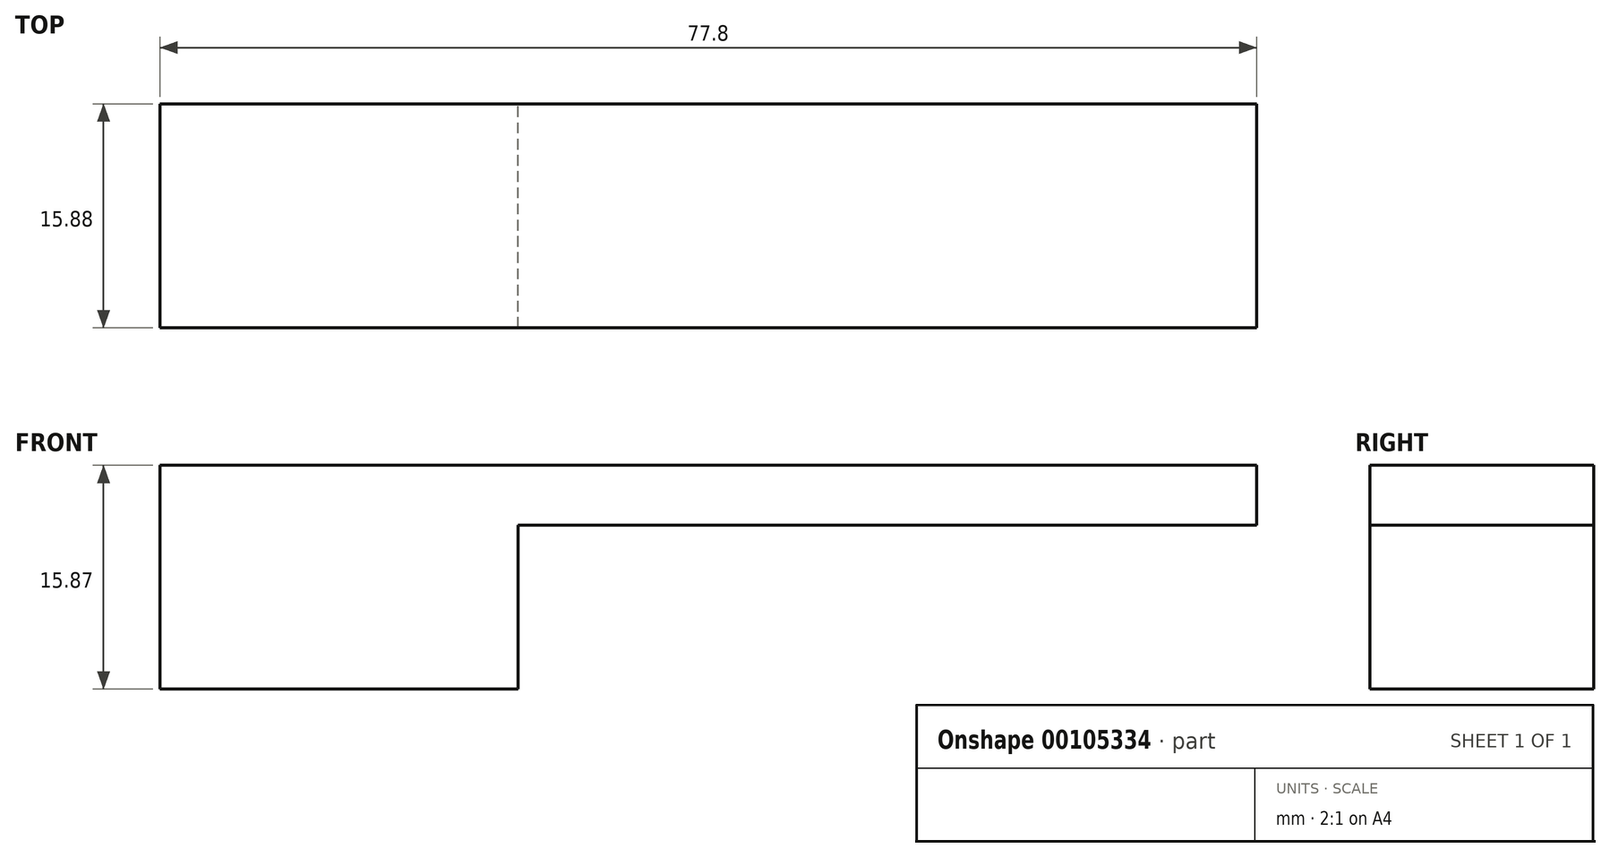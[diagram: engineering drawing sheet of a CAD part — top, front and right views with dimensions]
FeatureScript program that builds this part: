
annotation { "Feature Type Name" : "Feature", "Feature Type Description" : "" }
export const myFeature = defineFeature(function(context is Context, id is Id, definition is map)
    precondition{}
    {
        {
            var Q0;
            Q0=qCreatedBy(makeId("Front.planeOp"),FACE);
            var sketch = newSketch(context, id + "F0", { "sketchPlane" : qUnion([Q0])});
            skLineSegment(sketch, "E0.bottom", {"start": v(-56.23, 46.48) * mm, "end": v(-30.83, 46.48) * mm});
            skLineSegment(sketch, "E0.top", {"start": v(-56.23, 30.6) * mm, "end": v(-30.83, 30.6) * mm});
            skLineSegment(sketch, "E0.left", {"start": v(-56.23, 46.48) * mm, "end": v(-56.23, 30.6) * mm});
            skLineSegment(sketch, "E0.right", {"start": v(-30.83, 46.48) * mm, "end": v(-30.83, 30.6) * mm});
            skLineSegment(sketch, "E1", {"start": v(-56.23, 46.48) * mm, "end": v(21.56, 46.48) * mm});
            skLineSegment(sketch, "E2.bottom", {"start": v(-30.83, 46.48) * mm, "end": v(21.57, 46.48) * mm});
            skLineSegment(sketch, "E2.top", {"start": v(-30.83, 42.23) * mm, "end": v(21.57, 42.23) * mm});
            skLineSegment(sketch, "E2.left", {"start": v(-30.83, 46.48) * mm, "end": v(-30.83, 42.23) * mm});
            skLineSegment(sketch, "E2.right", {"start": v(21.57, 46.48) * mm, "end": v(21.57, 42.23) * mm});
            skSolve(sketch);
        }
        {
            var Q0;
            Q0=makeQuery(id+"F0.imprint","IMPRINT",FACE,{"disambiguationData":[TD([[makeQuery(id+"F0.imprint","IMPRINT",EDGE,{"derivedFrom":sQuery(id+"F0.wireOp",EDGE,"E0.top")}),1.0]])]});
            var Q1;
            Q1=makeQuery(id+"F0.imprint","IMPRINT",FACE,{"disambiguationData":[TD([[makeQuery(id+"F0.imprint","IMPRINT",EDGE,{"derivedFrom":sQuery(id+"F0.wireOp",EDGE,"E2.top")}),1.0]])]});
            extrude(context, id + "F1", {"entities" : qUnion([Q0, Q1]), "depth" : 15.88 * mm});
        }
    });
